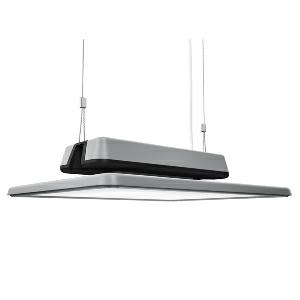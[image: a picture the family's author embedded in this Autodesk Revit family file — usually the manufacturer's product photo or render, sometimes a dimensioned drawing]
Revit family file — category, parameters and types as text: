
# Revit family: acaneo_-_hial_14000_840_n_ea_113549000-00737242_3bbf
name_source: partatom
category: Lighting Fixtures
units: mm (PartAtom-declared; Revit-internal decimal feet)

## family parameters
Cut with Voids When Loaded = No
Host = Face
Light Source = No
Part Type = Normal
Room Calculation Point = No
Round Connector Dimension = Use Diameter
Shared = No

## types (1)
- ACANEO - HIAL 14000/840/N/EA (1 x LED, 15000 lm, 4000K)
    Apparent Load = 90 VA
    Approval mark = CE
    CIE Flux Codes = 84 97 100 100 100
    Color Rendering = 80-89
    Color Temperature = 4000K
    Control Gear = Electronic ballast
    Default Elevation = 1800 mm
    Description = HIAL 14000/840/N/EA|High bay luminaire|light source: LED|work equipment: Electronic ballast|connected load: 220-240 V, 50/60 Hz|Power consumption: approx. 90 W|power factor: approx. 0,950|luminous flux: 15000 lm|luminous efficacy: 166 lm/W|colour temperature: Cold white, ca. 4000 K|color rendering index (CRI): >= 80|chromaticity tolerance:  3 SDCM|System of protection: IP 65|class of protection: I|technology: Switchable|luminaire body|material: Aluminium|surface: Powder coatet|colour: White aluminium|lamp cover: Acrylic (PMMA), Clear|weight (net): approx. 8.2 kg|mains lead: Built-in plug RST 25i3 Einbau|Fastening: Available separately|Accessory: Junction box (RST 2013)|minimum ambient temperature: -30 ░C|maximum ambient temperature: 50 ░C|glare control: Faceted optic|unified glare rating(4H 8H): <=  19|
    Frequency = 50 Hz, 60 Hz
    Height = 125 mm
    Lamp = 1 x LED
    Lamp Light Flux = 15000 lm
    Lamp count = 1
    Length = 480 mm
    Luminous efficacy = 167 lm/W
    Manufacturer = Waldmann
    ModVariant = No
    Model = 113549000-00737242
    Mounting Place = Ceiling
    Mounting Type = Pendant
    Number of Poles = 1
    OnlyDefault = Yes
    Power Factor = 1
    Product Name = ACANEO - HIAL 14000/840/N/EA
    Product group = High bay luminaire (industry)
    ProductGroupID = 901
    Protection Class = Protection class I
    Protection Degree = IP 65
    RLX_Detail_Level = 1
    RlxData = <blob elided: 30301 chars, md5=d00d5c10>
    Socket = socket
    Standby Power = 0 W
    System Light Flux = 15000 lm
    System Power = 90 W
    Type Comments = Product without accessories
    Type Image = acaneo-hial.jpg
    URL = http://relux.com
    VarID = ---
    Voltage = 230 V
    Voltage Range = 110-120 V, 220-240 V
    Weight = 0.00 kg
    Width = 405 mm

## geometry (parser evidence)
native form markers: Blend x4, Sweep x10
no freeform markers — native parametric forms only
